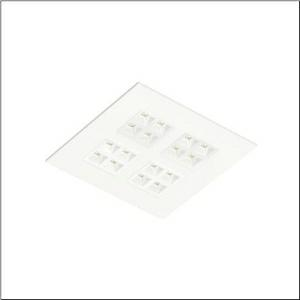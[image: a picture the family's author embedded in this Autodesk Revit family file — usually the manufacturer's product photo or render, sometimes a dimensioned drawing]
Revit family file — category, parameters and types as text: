
# Revit family: silica_31_square_51my6nms34wa
name_source: partatom
category: Lighting Fixtures
units: mm (PartAtom-declared; Revit-internal decimal feet)

## family parameters
Cut with Voids When Loaded = No
Host = Face
Light Source = No
Part Type = Normal
Room Calculation Point = No
Round Connector Dimension = Use Diameter
Shared = No

## types (1)
- --- (1 x LED, 6600 lm, 39 W, 3000K)
    Apparent Load = 39 VA
    CIE Flux Codes = 81 99 100 100 100
    Color Rendering = 80
    Color Temperature = 3000K
    Default Elevation = 1800 mm
    Description = Silica 31 Square, office luminaire, primary light control with lens, of PMMA, primary anti-glare with reflector, of PC, white, light emission: direct distribution, primary light characteristic: symmetric, installation type: lay-in mounting, LED, rated luminous flux: 4.580lm, luminous efficacy: 176lm/W, light colour: 830, colour temperature: 3000K, control gear: ON/OFF Multilumen, with terminal, 3-pole, mains connection: 220..240V, AC, 50/60Hz, rated input power: 26W, luminaire housing, of sheet steel, coated, traffic white (RAL 9016), module: M600, length: 595mm, width: 595mm, height: 43mm, protection rating (complete): IP20, insulation class (complete): insulation class II (safety insulation), certification: CE, impact resistance: IK03, permissible operating ambient temperature: -20..+35°C, standard: EN 50419, packaging unit: 1 piece
    Height = 0 mm  [stored 0 ft]
    Lamp = 1 x LED
    Lamp Light Flux = 6600 lm
    Lamp Power = 39 W
    Lamp count = 1
    Length = 595 mm
    Luminous efficacy = 169 lm/W
    Manufacturer = Siteco
    ModVariant = No
    Model = 51MY6NMS34WA
    Mounting Place = Ceiling
    Mounting Type = Recessed
    Number of Poles = 1
    OnlyDefault = Yes
    Power Factor = 1
    Product Name = Silica 31 Square
    Product group = office luminaire | ceiling recessed
    ProductGroupID = 400
    Protection Class = Protection class II
    Protection Degree = IP 20
    RLX_Detail_Level = 1
    RLX_Emergency_Light_Flux = 0 lm
    RLX_Emergency_Type = 0
    RLX_Emergency_Type_DB = No
    RlxData = <blob elided: 28549 chars, md5=98cb9018>
    Socket = socket
    Standby Power = 0 W
    System Light Flux = 6600 lm
    System Power = 39 W
    Type Comments = factory setting: luminous flux: 100 % | (ON | ON | ON | ON) | 1100 mA
    Type Image = l_1313651.jpg
    URL = http://relux.com
    VarID = @adj_043019
    Voltage = 0 V
    Weight = 0.00 kg
    Width = 595 mm

note: [stored X ft] marks values corroborated as IEEE doubles in the binary element streams (Revit-internal decimal feet)

## geometry (parser evidence)
native form markers: Blend x4, Sweep x9
no freeform markers — native parametric forms only
